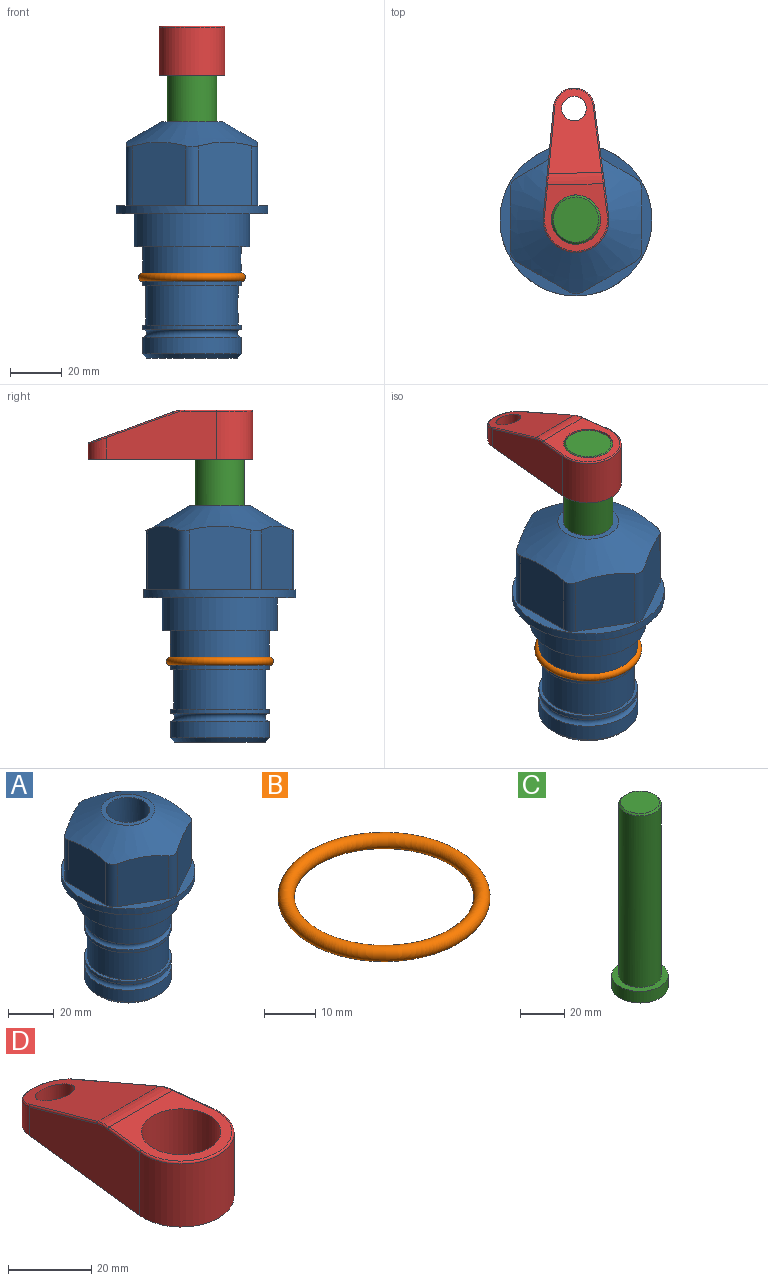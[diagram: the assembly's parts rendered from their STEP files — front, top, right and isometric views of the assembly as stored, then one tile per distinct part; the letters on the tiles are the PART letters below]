
ASSEMBLY  parts=4 mates=2
PART A: 36 faces, bbox 58.7x58.7x91.2 mm
  f0: cylinder r=17.78mm len=35.56mm, axis (0,0,1), area 1670.8mm2, adj f23,f24,f31
  f1: cylinder r=19.05mm len=38.1mm, axis (0,0,1), area 1191.9mm2, adj f26,f27,f30
  f2: plane 58.66x58.66mm, normal (0,0,-1), area 1150.6mm2, adj f3,f28
  f3: cylinder r=29.33mm len=58.66mm, axis (0,0,-1), area 585.1mm2, adj f2,f4
  f4: plane 58.66x58.66mm, normal (0,0,1), area 475.9mm2, adj f3,f5,f6,f7,f8,f9,f10,f11
  f5: plane 24.5x20.32mm, normal (-0.5,0.87,0), area 562.8mm2, adj f4,f15,f16,f17
  f6: plane 24.5x20.32mm, normal (0.5,0.87,0), area 562.8mm2, adj f4,f14,f15,f17
  f7: plane 24.5x23.48mm, normal (1,0,0), area 562.8mm2, adj f4,f13,f14,f17
  f8: plane 24.5x20.32mm, normal (0.5,-0.87,0), area 562.8mm2, adj f4,f12,f13,f17
  f9: plane 24.5x20.32mm, normal (-0.5,-0.87,0), area 562.8mm2, adj f4,f11,f12,f17
  f10: plane 24.5x23.48mm, normal (-1,0,0), area 562.8mm2, adj f4,f11,f16,f17
  f11: cylinder r=5.08mm len=23.01mm, axis (0,0,-1), area 121.2mm2, adj f4,f9,f10,f17
  f12: cylinder r=5.08mm len=23.01mm, axis (0,0,-1), area 121.2mm2, adj f4,f8,f9,f17
  f13: cylinder r=5.08mm len=23.01mm, axis (0,0,-1), area 121.2mm2, adj f4,f7,f8,f17
  f14: cylinder r=5.08mm len=23.01mm, axis (0,0,-1), area 121.2mm2, adj f4,f6,f7,f17
  f15: cylinder r=5.08mm len=23.01mm, axis (0,0,-1), area 121.2mm2, adj f4,f5,f6,f17
  f16: cylinder r=5.08mm len=23.01mm, axis (0,0,-1), area 121.2mm2, adj f4,f5,f10,f17
  f17: cone r=11.73mm half-angle=60deg, axis (0,0,-1), area 2071.8mm2, adj f5,f6,f7,f8,f9,f10,f11,f12
  f18: plane 23.46x23.46mm, normal (0,0,1), area 147.4mm2, adj f17,f35
  f19: plane 34.93x34.93mm, normal (0,0,-1), area 958mm2, adj f29
  f20: cylinder r=19.05mm len=38.1mm, axis (0,0,1), area 760.1mm2, adj f21,f29
  f21: torus R=19.05mm, axis (0,0,1), area 565.3mm2, adj f20,f22
  f22: cylinder r=19.05mm len=38.1mm, axis (0,0,1), area 190mm2, adj f21,f23
  f23: plane 38.1x38.1mm, normal (0,0,1), area 146.9mm2, adj f0,f22
  f24: plane 38.1x38.1mm, normal (0,0,-1), area 146.9mm2, adj f0,f25
  f25: cylinder r=19.05mm len=38.1mm, axis (0,0,1), area 190mm2, adj f24,f26
  f26: torus R=19.05mm, axis (0,0,1), area 565.3mm2, adj f1,f25
  f27: plane 44.45x44.45mm, normal (0,0,-1), area 411.7mm2, adj f1,f28
  f28: cylinder r=22.23mm len=44.45mm, axis (0,0,1), area 1773.5mm2, adj f2,f27
  f29: cone r=19.05mm half-angle=45deg, axis (0,0,1), area 257.5mm2, adj f19,f20
  f30: cylinder r=3.17mm len=6.75mm, axis (-1,0,0), area 128mm2, adj f1,f33
  f31: cylinder r=3.17mm len=6.35mm, axis (-1,0,0), area 102.5mm2, adj f0,f33
  f32: plane 25.4x25.4mm, normal (0,0,1), area 506.7mm2, adj f33
  f33: cylinder r=12.7mm len=66.42mm, axis (0,0,-1), area 5236.2mm2, adj f30,f31,f32,f34
  f34: cone r=9.53mm half-angle=30deg, axis (0,0,-1), area 443.4mm2, adj f33,f35
  f35: cylinder r=9.53mm len=19.05mm, axis (0,0,-1), area 849mm2, adj f18,f34
PART B: 1 faces, bbox 44.7x44.7x3.2 mm
  f0: torus R=19.05mm, axis (0,0,1), area 1193.9mm2
PART C: 6 faces, bbox 25.4x25.4x101.6 mm
  f0: plane 17.46x17.46mm, normal (0,0,1), area 239.5mm2, adj f5
  f1: plane 25.4x25.4mm, normal (0,0,-1), area 506.7mm2, adj f2
  f2: cylinder r=12.7mm len=25.4mm, axis (0,0,1), area 506.7mm2, adj f1,f3
  f3: plane 25.4x25.4mm, normal (0,0,1), area 221.7mm2, adj f2,f4
  f4: cylinder r=9.53mm len=94.46mm, axis (0,0,1), area 5653mm2, adj f3,f5
  f5: cone r=8.73mm half-angle=45deg, axis (0,0,-1), area 64.4mm2, adj f0,f4
PART D: 44 faces, bbox 27.5x64.5x19.1 mm
  f0: plane 2.3x0.95mm, normal (0,0,-1), area 1mm2, adj f25,f30,f34
  f1: plane 63.5x25.4mm, normal (0,0,-1), area 561.7mm2, adj f2,f3,f4,f5,f6,f7,f19,f20
  f2: cylinder r=12.7mm len=25.4mm, axis (0,0,-1), area 792.2mm2, adj f1,f3,f5,f13
  f3: plane 42.33x18.54mm, normal (0.99,0.11,0), area 647mm2, adj f1,f2,f4,f11,f12,f14
  f4: cylinder r=7.94mm len=15.78mm, axis (0,0,-1), area 158.6mm2, adj f1,f3,f5,f16
  f5: plane 42.33x18.54mm, normal (-0.99,0.11,0), area 647mm2, adj f1,f2,f4,f15,f17,f18
  f6: cylinder r=9.53mm len=19.05mm, axis (0,0,-1), area 1140.1mm2, adj f1,f8
  f7: cylinder r=4.76mm len=10.98mm, axis (0,0,-1), area 276.1mm2, adj f1,f9
  f8: plane 25.83x24.38mm, normal (0,0,1), area 262.2mm2, adj f6,f10,f11,f13,f15
  f9: plane 32.49x20.55mm, normal (0,0.34,0.94), area 489.9mm2, adj f7,f10,f14,f16,f18
  f10: cylinder r=12.7mm len=21.49mm, axis (-1,0,0), area 93.2mm2, adj f8,f9,f12,f17
  f11: cylinder r=0.51mm len=12.34mm, axis (0.11,-0.99,0), area 9.9mm2, adj f3,f8,f12,f13
  f12: bspline ~7.62x1.64mm, area 3.5mm2, adj f3,f10,f11,f14
  f13: torus R=12.19mm, axis (0,0,1), area 33.6mm2, adj f2,f8,f11,f15
  f14: cylinder r=0.51mm len=26.01mm, axis (0.1,-0.93,0.34), area 21.6mm2, adj f3,f9,f12,f16
  f15: cylinder r=0.51mm len=12.34mm, axis (0.11,0.99,0), area 9.9mm2, adj f5,f8,f13,f17
  f16: bspline ~15.78x7.05mm, area 15.7mm2, adj f4,f9,f14,f18
  f17: bspline ~7.62x1.64mm, area 3.5mm2, adj f5,f10,f15,f18
  f18: cylinder r=0.51mm len=26.01mm, axis (0.1,0.93,-0.34), area 21.6mm2, adj f5,f9,f16,f17
  f19: plane 21.6x14.29mm, normal (-0.99,-0.11,0), area 242.6mm2, adj f1,f26,f28,f34,f36,f38
  f20: plane 21.6x14.29mm, normal (0.99,-0.11,0), area 242.6mm2, adj f1,f27,f29,f37,f39,f41
  f21: cylinder r=12.7mm len=14.29mm, axis (0,0,-1), area 173.2mm2, adj f1,f26,f27,f30,f31,f33
  f22: cylinder r=7.94mm len=7.63mm, axis (0,0,-1), area 53.8mm2, adj f1,f28,f29,f42
  f23: plane 2.3x0.95mm, normal (0,0,-1), area 1mm2, adj f25,f33,f37
  f24: plane 17.94x12.32mm, normal (0,-0.34,-0.94), area 191.2mm2, adj f25,f38,f41,f42
  f25: cylinder r=9.53mm len=12.93mm, axis (-1,0,0), area 37.5mm2, adj f0,f23,f24,f31,f36,f39
  f26: cylinder r=1.59mm len=14.29mm, axis (0,0,-1), area 49mm2, adj f1,f19,f21,f32
  f27: cylinder r=1.59mm len=14.29mm, axis (0,0,-1), area 49mm2, adj f1,f20,f21,f35
  f28: cylinder r=1.59mm len=7.28mm, axis (0,0,-1), area 22.1mm2, adj f1,f19,f22,f40
  f29: cylinder r=1.59mm len=7.28mm, axis (0,0,-1), area 22.1mm2, adj f1,f20,f22,f43
  f30: torus R=14.29mm, axis (0,0,1), area 5.8mm2, adj f0,f21,f31,f32
  f31: bspline ~11.06x2.73mm, area 20.8mm2, adj f21,f25,f30,f33
  f32: sphere r=1.59mm, area 5.4mm2, adj f26,f30,f34
  f33: torus R=14.29mm, axis (0,0,1), area 5.8mm2, adj f21,f23,f31,f35
  f34: cylinder r=1.59mm len=1.68mm, axis (-0.11,0.99,0), area 2.4mm2, adj f0,f19,f32,f36
  f35: sphere r=1.59mm, area 5.4mm2, adj f27,f33,f37
  f36: bspline ~5.82x2.33mm, area 7.7mm2, adj f19,f25,f34,f38
  f37: cylinder r=1.59mm len=1.68mm, axis (0.11,0.99,0), area 2.4mm2, adj f20,f23,f35,f39
  f38: cylinder r=1.59mm len=18.33mm, axis (0.1,-0.93,0.34), area 46.7mm2, adj f19,f24,f36,f40
  f39: bspline ~5.82x2.33mm, area 7.7mm2, adj f20,f25,f37,f41
  f40: sphere r=1.59mm, area 3.6mm2, adj f28,f38,f42
  f41: cylinder r=1.59mm len=18.33mm, axis (0.1,0.93,-0.34), area 46.7mm2, adj f20,f24,f39,f43
  f42: bspline ~8.31x1.84mm, area 15.3mm2, adj f22,f24,f40,f43
  f43: sphere r=1.59mm, area 3.6mm2, adj f29,f41,f42
PLACE A t=(-1.44,-0.08,0.69)mm fixed
PLACE B t=(-1.44,-0.08,0.69)mm
PLACE C rot(axis=(0,0,1),1deg) t=(-1.44,-0.08,-0.51)mm
PLACE D rot(axis=(0,0,1),1deg) t=(-1.44,-0.08,54.1)mm
MATE cylindrical C.f2 <-> A.f0  axis (0,0,1) through (-1.44,-0.08,25.13)mm
MATE fastened D.f2 <-> C.f2  axis (0,0,-1) through (-1.44,-0.08,73.15)mm
